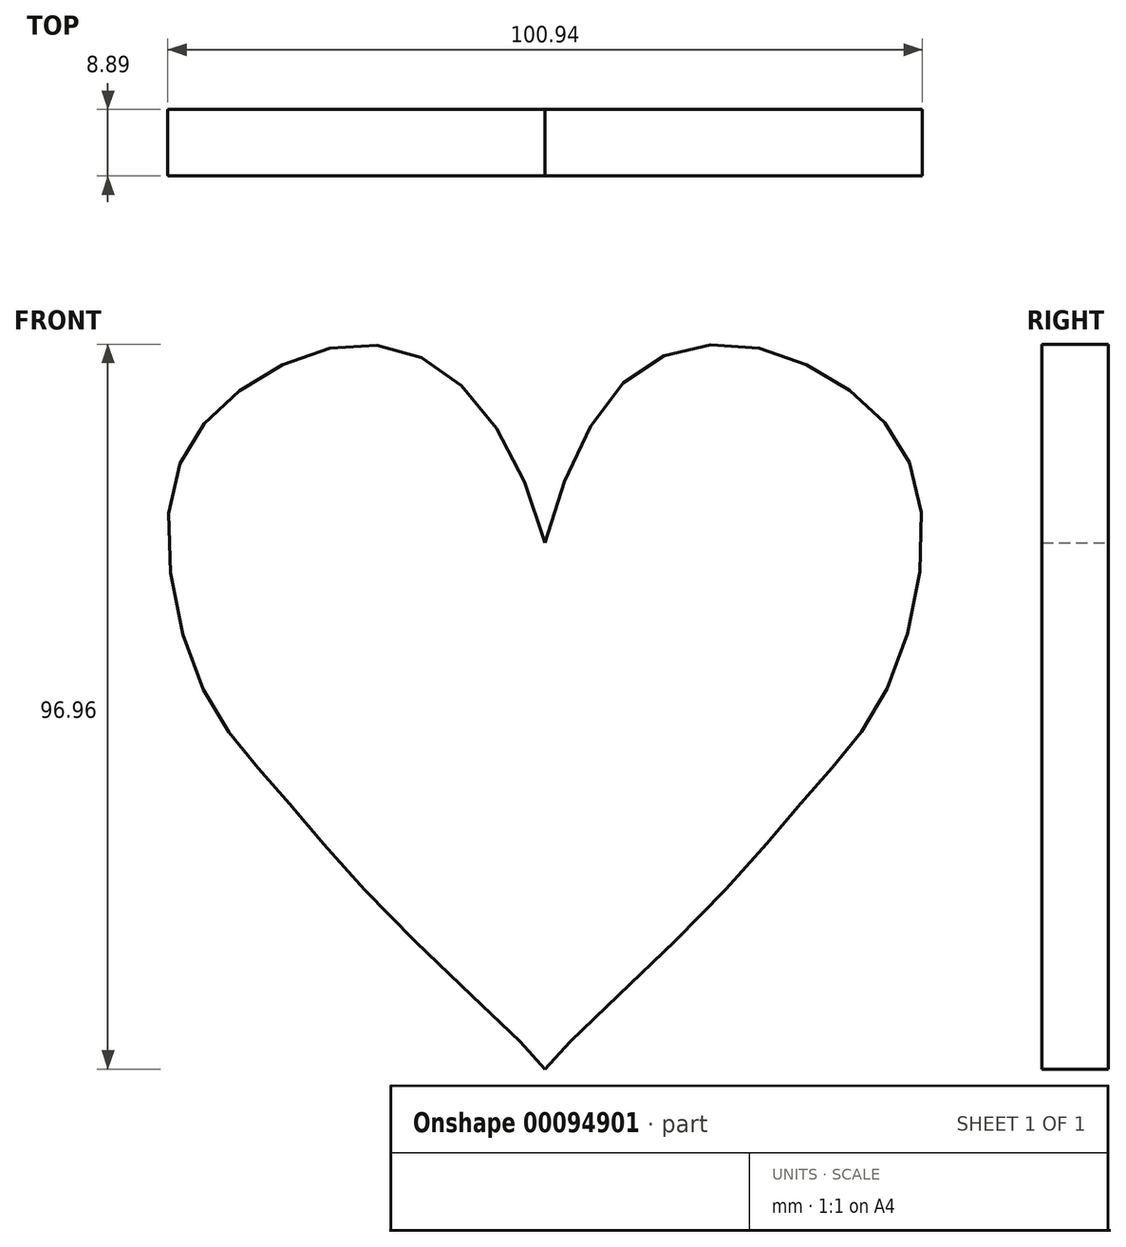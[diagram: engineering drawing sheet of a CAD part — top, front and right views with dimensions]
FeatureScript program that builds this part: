
annotation { "Feature Type Name" : "Feature", "Feature Type Description" : "" }
export const myFeature = defineFeature(function(context is Context, id is Id, definition is map)
    precondition{}
    {
        {
            var Q0;
            Q0=qCreatedBy(makeId("Front.planeOp"),FACE);
            var sketch = newSketch(context, id + "F0", { "sketchPlane" : qUnion([Q0])});
            skFitSpline(sketch, "E0", {"points": [v(0.06, 12.14) * mm, v(11.26, 34.18) * mm, v(26.4, 38.53) * mm, v(42.3, 31.36) * mm, v(50.25, 17.63) * mm, v(45.9, -7.2) * mm, v(36.26, -20.47) * mm, v(19.9, -38.75) * mm, v(0.06, -58.26) * mm, v(0.06, -58.98) * mm], "startDerivative": vector(51.6, 197.91) * mm, "endDerivative": vector(16.47, -31.24) * mm});
            skFitSpline(sketch, "E1.MirrorCS", {"points": [v(0.06, 12.14) * mm, v(-11.87, 33.82) * mm, v(-26.28, 38.59) * mm, v(-42.18, 31.36) * mm, v(-50.13, 17.63) * mm, v(-45.8, -7.2) * mm, v(-36.15, -20.47) * mm, v(-19.78, -38.75) * mm, v(0.06, -58.26) * mm, v(0.06, -58.98) * mm], "startDerivative": vector(-51.6, 197.91) * mm, "endDerivative": vector(-16.47, -31.24) * mm});
            skSolve(sketch);
        }
        {
            var Q0;
            {var subQ0=sQuery(id+"F0.wireOp",EDGE,"E1.MirrorCS");var subQ1=sQuery(id+"F0.wireOp",EDGE,"E0");var subQ2=makeQuery(id+"F0.imprint","INTERSECT",VERTEX,{"disambiguationData":[OD(0.0)],"derivedFrom":[subQ1,subQ0]});Q0=makeQuery(id+"F0.imprint","IMPRINT",FACE,{"disambiguationData":[TD([[makeQuery(id+"F0.imprint","IMPRINT",EDGE,{"disambiguationData":[TD([[subQ2,-1.0]])],"derivedFrom":subQ1}),-1.0]])]});}
            extrude(context, id + "F1", {"entities" : qUnion([Q0]), "depth" : 8.9 * mm});
        }
    });
